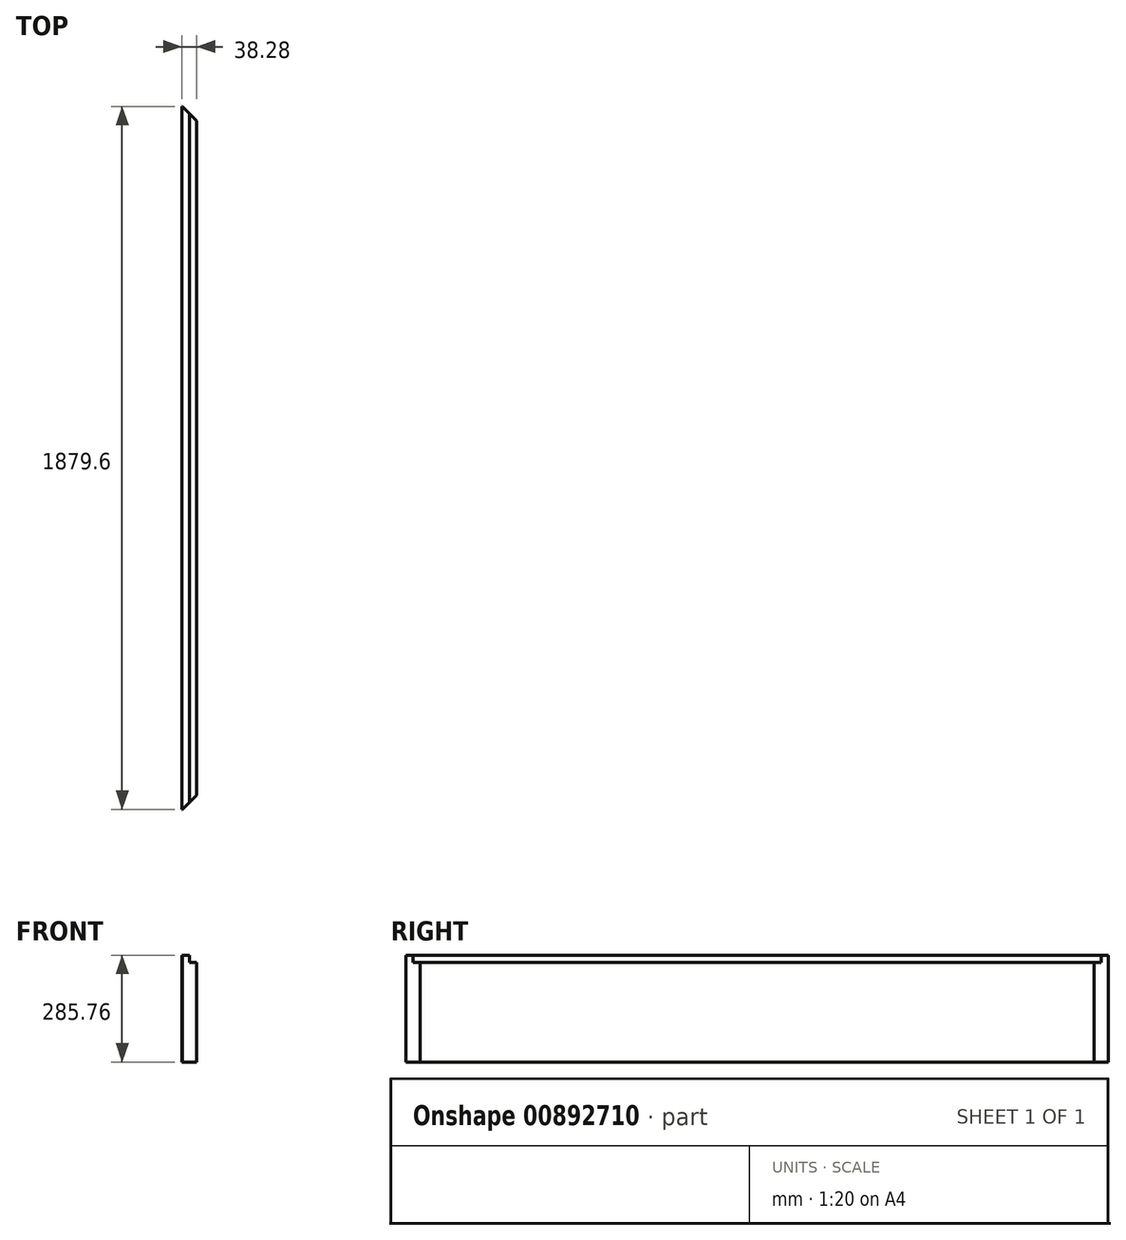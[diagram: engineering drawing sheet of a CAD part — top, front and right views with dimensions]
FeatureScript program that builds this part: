
annotation { "Feature Type Name" : "Feature", "Feature Type Description" : "" }
export const myFeature = defineFeature(function(context is Context, id is Id, definition is map)
    precondition{}
    {
        {
            var Q0;
            Q0=qCreatedBy(makeId("Front.planeOp"),FACE);
            var sketch = newSketch(context, id + "F0", { "sketchPlane" : qUnion([Q0])});
            skLineSegment(sketch, "E0.bottom", {"start": v(19.14, 142.87) * mm, "end": v(-19.14, 142.87) * mm});
            skLineSegment(sketch, "E0.top", {"start": v(19.14, -142.88) * mm, "end": v(-19.14, -142.88) * mm});
            skLineSegment(sketch, "E0.left", {"start": v(19.14, 142.87) * mm, "end": v(19.14, -142.88) * mm});
            skLineSegment(sketch, "E0.right", {"start": v(-19.14, 142.87) * mm, "end": v(-19.14, -142.88) * mm});
            skPoint(sketch, "E0.middle", {"position": v(0, 0) * mm});
            skSolve(sketch);
        }
        {
            var Q0;
            Q0 = qSketchRegion(id + "F0", true);
            extrude(context, id + "F1", {"entities" : qUnion([Q0]), "depth" : 1879.6 * mm, "offsetDistance" : 25.4 * mm});
        }
        {
            var Q0;
            Q0=makeQuery(id+"F1.opExtrude","CAP_EDGE",EDGE,{"disambiguationData":[OSD([sQuery(id+"F0.wireOp",EDGE,"E0.left")])],"isStart":false});
            var Q1;
            Q1=makeQuery(id+"F1.opExtrude","CAP_EDGE",EDGE,{"disambiguationData":[OSD([sQuery(id+"F0.wireOp",EDGE,"E0.left")])],"isStart":true});
            chamfer(context, id + "F2", {"entities" : qUnion([Q0, Q1]), "width" : 38.1 * mm, "tangentPropagation" : true});
        }
        {
            var Q0;
            Q0=makeQuery(id+"F1.opExtrude","SWEPT_FACE",FACE,{"disambiguationData":[OSD([sQuery(id+"F0.wireOp",EDGE,"E0.left")])]});
            var sketch = newSketch(context, id + "F3", { "sketchPlane" : qUnion([Q0])});
            skLineSegment(sketch, "E1.bottom", {"start": v(-1860.55, 142.87) * mm, "end": v(-19.05, 142.87) * mm});
            skLineSegment(sketch, "E1.top", {"start": v(-1860.55, 123.83) * mm, "end": v(-19.05, 123.83) * mm});
            skLineSegment(sketch, "E1.left", {"start": v(-1860.55, 142.87) * mm, "end": v(-1860.55, 123.83) * mm});
            skLineSegment(sketch, "E1.right", {"start": v(-19.05, 142.87) * mm, "end": v(-19.05, 123.83) * mm});
            skSolve(sketch);
        }
        {
            var Q0;
            Q0 = qSketchRegion(id + "F3", true);
            extrude(context, id + "F4", {"entities" : qUnion([Q0]), "operationType" : NewBodyOperationType.REMOVE, "oppositeDirection" : true, "depth" : 19.05 * mm, "offsetDistance" : 25.4 * mm});
        }
    });
